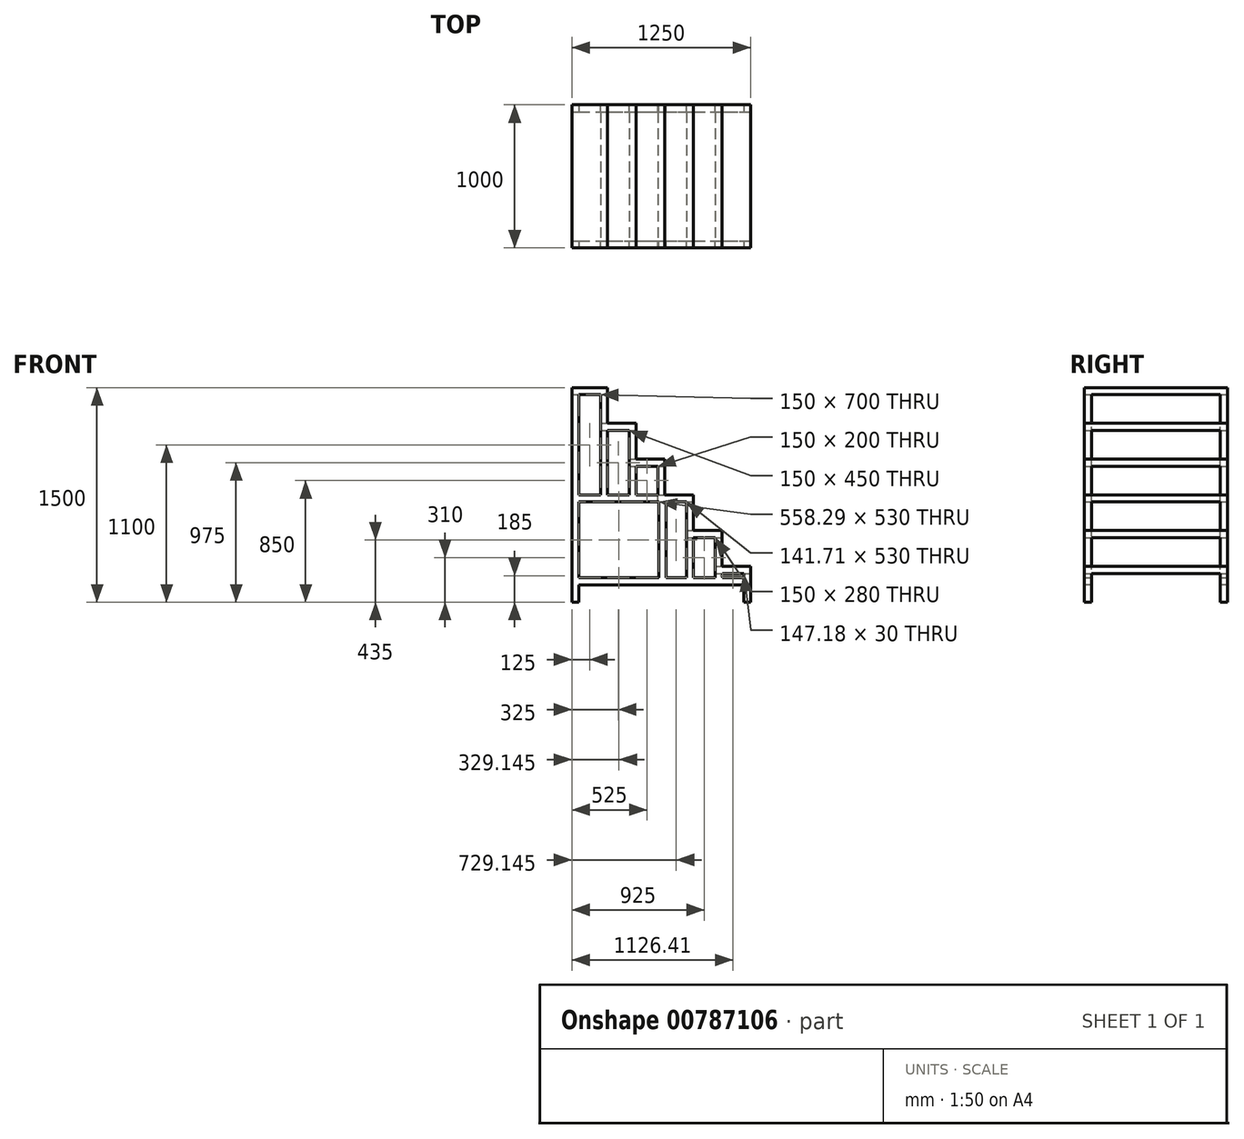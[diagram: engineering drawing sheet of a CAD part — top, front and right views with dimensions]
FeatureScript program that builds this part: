
annotation { "Feature Type Name" : "Feature", "Feature Type Description" : "" }
export const myFeature = defineFeature(function(context is Context, id is Id, definition is map)
    precondition{}
    {
        {
            var Q0;
            Q0=qCreatedBy(makeId("Front.planeOp"),FACE);
            var sketch = newSketch(context, id + "F0", { "sketchPlane" : qUnion([Q0])});
            skLineSegment(sketch, "E0.bottom", {"start": v(0, 0) * mm, "end": v(1250, 0) * mm});
            skLineSegment(sketch, "E0.top", {"start": v(0, 250) * mm, "end": v(1250, 250) * mm});
            skLineSegment(sketch, "E0.left", {"start": v(0, 0) * mm, "end": v(0, 250) * mm});
            skLineSegment(sketch, "E0.right", {"start": v(1250, 0) * mm, "end": v(1250, 250) * mm});
            skLineSegment(sketch, "E1.bottom", {"start": v(0, 250) * mm, "end": v(1050, 250) * mm});
            skLineSegment(sketch, "E1.top", {"start": v(0, 500) * mm, "end": v(1050, 500) * mm});
            skLineSegment(sketch, "E1.left", {"start": v(0, 250) * mm, "end": v(0, 500) * mm});
            skLineSegment(sketch, "E1.right", {"start": v(1050, 250) * mm, "end": v(1050, 500) * mm});
            skLineSegment(sketch, "E2.bottom", {"start": v(0, 500) * mm, "end": v(850, 500) * mm});
            skLineSegment(sketch, "E2.top", {"start": v(0, 750) * mm, "end": v(850, 750) * mm});
            skLineSegment(sketch, "E2.left", {"start": v(0, 500) * mm, "end": v(0, 750) * mm});
            skLineSegment(sketch, "E2.right", {"start": v(850, 500) * mm, "end": v(850, 750) * mm});
            skLineSegment(sketch, "E3.bottom", {"start": v(0, 750) * mm, "end": v(650, 750) * mm});
            skLineSegment(sketch, "E3.top", {"start": v(0, 1000) * mm, "end": v(650, 1000) * mm});
            skLineSegment(sketch, "E3.left", {"start": v(0, 750) * mm, "end": v(0, 1000) * mm});
            skLineSegment(sketch, "E3.right", {"start": v(650, 750) * mm, "end": v(650, 1000) * mm});
            skLineSegment(sketch, "E4.bottom", {"start": v(0, 1000) * mm, "end": v(450, 1000) * mm});
            skLineSegment(sketch, "E4.top", {"start": v(0, 1250) * mm, "end": v(450, 1250) * mm});
            skLineSegment(sketch, "E4.left", {"start": v(0, 1000) * mm, "end": v(0, 1250) * mm});
            skLineSegment(sketch, "E4.right", {"start": v(450, 1000) * mm, "end": v(450, 1250) * mm});
            skLineSegment(sketch, "E5.bottom", {"start": v(0, 1250) * mm, "end": v(250, 1250) * mm});
            skLineSegment(sketch, "E5.top", {"start": v(0, 1500) * mm, "end": v(250, 1500) * mm});
            skLineSegment(sketch, "E5.left", {"start": v(0, 1250) * mm, "end": v(0, 1500) * mm});
            skLineSegment(sketch, "E5.right", {"start": v(250, 1250) * mm, "end": v(250, 1500) * mm});
            skSolve(sketch);
        }
        {
            var Q0;
            Q0 = qSketchRegion(id + "F0", true);
            extrude(context, id + "F1", {"entities" : qUnion([Q0]), "depth" : 1000 * mm, "offsetDistance" : 25 * mm});
        }
        {
            var Q0;
            Q0=makeQuery(id+"F1.opExtrude","SWEPT_FACE",FACE,{"disambiguationData":[OSD([sQuery(id+"F0.wireOp",EDGE,"E0.left"),sQuery(id+"F0.wireOp",EDGE,"E1.left"),sQuery(id+"F0.wireOp",EDGE,"E2.left"),sQuery(id+"F0.wireOp",EDGE,"E3.left"),sQuery(id+"F0.wireOp",EDGE,"E4.left"),sQuery(id+"F0.wireOp",EDGE,"E5.left")])]});
            shell(context, id + "F2", {"entities" : qUnion([Q0]), "thickness" : 50 * mm});
        }
        {
            var Q0;
            Q0=makeQuery(id+"F1.opExtrude","CAP_FACE",FACE,{"disambiguationData":[OSD([sQuery(id+"F0.wireOp",EDGE,"E0.bottom"),sQuery(id+"F0.wireOp",EDGE,"E0.top"),sQuery(id+"F0.wireOp",EDGE,"E0.left"),sQuery(id+"F0.wireOp",EDGE,"E0.right"),sQuery(id+"F0.wireOp",EDGE,"E1.top"),sQuery(id+"F0.wireOp",EDGE,"E1.left"),sQuery(id+"F0.wireOp",EDGE,"E1.right"),sQuery(id+"F0.wireOp",EDGE,"E2.top"),sQuery(id+"F0.wireOp",EDGE,"E2.left"),sQuery(id+"F0.wireOp",EDGE,"E2.right"),sQuery(id+"F0.wireOp",EDGE,"E3.top"),sQuery(id+"F0.wireOp",EDGE,"E3.left"),sQuery(id+"F0.wireOp",EDGE,"E3.right"),sQuery(id+"F0.wireOp",EDGE,"E4.top"),sQuery(id+"F0.wireOp",EDGE,"E4.left"),sQuery(id+"F0.wireOp",EDGE,"E4.right"),sQuery(id+"F0.wireOp",EDGE,"E5.top"),sQuery(id+"F0.wireOp",EDGE,"E5.left"),sQuery(id+"F0.wireOp",EDGE,"E5.right")])],"isStart":false});
            var sketch = newSketch(context, id + "F3", { "sketchPlane" : qUnion([Q0])});
            skLineSegment(sketch, "E6.bottom", {"start": v(50, 0) * mm, "end": v(1200, 0) * mm});
            skLineSegment(sketch, "E6.top", {"start": v(50, 120) * mm, "end": v(1200, 120) * mm});
            skLineSegment(sketch, "E6.left", {"start": v(50, 0) * mm, "end": v(50, 120) * mm});
            skLineSegment(sketch, "E6.right", {"start": v(1200, 0) * mm, "end": v(1200, 120) * mm});
            skSolve(sketch);
        }
        {
            var Q0;
            Q0=makeQuery(id+"F3.imprint","IMPRINT",FACE,{"disambiguationData":[TD([[makeQuery(id+"F3.imprint","IMPRINT",EDGE,{"derivedFrom":sQuery(id+"F3.wireOp",EDGE,"E6.bottom")}),1.0]])]});
            extrude(context, id + "F4", {"entities" : qUnion([Q0]), "operationType" : NewBodyOperationType.REMOVE, "oppositeDirection" : true, "depth" : 1100 * mm, "offsetDistance" : 25 * mm});
        }
        {
            var Q0;
            Q0=makeQuery(id+"F1.opExtrude","SWEPT_FACE",FACE,{"disambiguationData":[OSD([sQuery(id+"F0.wireOp",EDGE,"E0.right")])]});
            var sketch = newSketch(context, id + "F5", { "sketchPlane" : qUnion([Q0])});
            skLineSegment(sketch, "E7.bottom", {"start": v(-950, 0) * mm, "end": v(-50, 0) * mm});
            skLineSegment(sketch, "E7.top", {"start": v(-950, 200) * mm, "end": v(-50, 200) * mm});
            skLineSegment(sketch, "E7.left", {"start": v(-950, 0) * mm, "end": v(-950, 200) * mm});
            skLineSegment(sketch, "E7.right", {"start": v(-50, 0) * mm, "end": v(-50, 200) * mm});
            skSolve(sketch);
        }
        {
            var Q0;
            Q0 = qSketchRegion(id + "F5", true);
            extrude(context, id + "F6", {"entities" : qUnion([Q0]), "operationType" : NewBodyOperationType.REMOVE, "oppositeDirection" : true, "depth" : 5000 * mm, "offsetDistance" : 25 * mm});
        }
        {
            var Q0;
            Q0=makeQuery(id+"F1.opExtrude","SWEPT_FACE",FACE,{"disambiguationData":[OSD([sQuery(id+"F0.wireOp",EDGE,"E1.right")])]});
            var sketch = newSketch(context, id + "F7", { "sketchPlane" : qUnion([Q0])});
            skLineSegment(sketch, "E8.bottom", {"start": v(-950, 250) * mm, "end": v(-50, 250) * mm});
            skLineSegment(sketch, "E8.top", {"start": v(-950, 450) * mm, "end": v(-50, 450) * mm});
            skLineSegment(sketch, "E8.left", {"start": v(-950, 250) * mm, "end": v(-950, 450) * mm});
            skLineSegment(sketch, "E8.right", {"start": v(-50, 250) * mm, "end": v(-50, 450) * mm});
            skSolve(sketch);
        }
        {
            var Q0;
            Q0 = qSketchRegion(id + "F7", true);
            extrude(context, id + "F8", {"entities" : qUnion([Q0]), "operationType" : NewBodyOperationType.REMOVE, "oppositeDirection" : true, "depth" : 300 * mm, "offsetDistance" : 25 * mm});
        }
        {
            var Q0;
            Q0=makeQuery(id+"F1.opExtrude","SWEPT_FACE",FACE,{"disambiguationData":[OSD([sQuery(id+"F0.wireOp",EDGE,"E2.right")])]});
            var sketch = newSketch(context, id + "F9", { "sketchPlane" : qUnion([Q0])});
            skLineSegment(sketch, "E9.bottom", {"start": v(-950, 500) * mm, "end": v(-50, 500) * mm});
            skLineSegment(sketch, "E9.top", {"start": v(-950, 700) * mm, "end": v(-50, 700) * mm});
            skLineSegment(sketch, "E9.left", {"start": v(-950, 500) * mm, "end": v(-950, 700) * mm});
            skLineSegment(sketch, "E9.right", {"start": v(-50, 500) * mm, "end": v(-50, 700) * mm});
            skSolve(sketch);
        }
        {
            var Q0;
            Q0 = qSketchRegion(id + "F9", true);
            extrude(context, id + "F10", {"entities" : qUnion([Q0]), "operationType" : NewBodyOperationType.REMOVE, "oppositeDirection" : true, "depth" : 300 * mm, "offsetDistance" : 25 * mm});
        }
        {
            var Q0;
            Q0=makeQuery(id+"F1.opExtrude","SWEPT_FACE",FACE,{"disambiguationData":[OSD([sQuery(id+"F0.wireOp",EDGE,"E3.right")])]});
            var sketch = newSketch(context, id + "F11", { "sketchPlane" : qUnion([Q0])});
            skLineSegment(sketch, "E10.bottom", {"start": v(-950, 750) * mm, "end": v(-50, 750) * mm});
            skLineSegment(sketch, "E10.top", {"start": v(-950, 950) * mm, "end": v(-50, 950) * mm});
            skLineSegment(sketch, "E10.left", {"start": v(-950, 750) * mm, "end": v(-950, 950) * mm});
            skLineSegment(sketch, "E10.right", {"start": v(-50, 750) * mm, "end": v(-50, 950) * mm});
            skSolve(sketch);
        }
        {
            var Q0;
            Q0 = qSketchRegion(id + "F11", true);
            extrude(context, id + "F12", {"entities" : qUnion([Q0]), "operationType" : NewBodyOperationType.REMOVE, "oppositeDirection" : true, "depth" : 300 * mm, "offsetDistance" : 25 * mm});
        }
        {
            var Q0;
            Q0=makeQuery(id+"F1.opExtrude","SWEPT_FACE",FACE,{"disambiguationData":[OSD([sQuery(id+"F0.wireOp",EDGE,"E4.right")])]});
            var sketch = newSketch(context, id + "F13", { "sketchPlane" : qUnion([Q0])});
            skLineSegment(sketch, "E11.bottom", {"start": v(-950, 1000) * mm, "end": v(-50, 1000) * mm});
            skLineSegment(sketch, "E11.top", {"start": v(-950, 1200) * mm, "end": v(-50, 1200) * mm});
            skLineSegment(sketch, "E11.left", {"start": v(-950, 1000) * mm, "end": v(-950, 1200) * mm});
            skLineSegment(sketch, "E11.right", {"start": v(-50, 1000) * mm, "end": v(-50, 1200) * mm});
            skSolve(sketch);
        }
        {
            var Q0;
            Q0 = qSketchRegion(id + "F13", true);
            extrude(context, id + "F14", {"entities" : qUnion([Q0]), "operationType" : NewBodyOperationType.REMOVE, "oppositeDirection" : true, "depth" : 300 * mm, "offsetDistance" : 25 * mm});
        }
        {
            var Q0;
            Q0=makeQuery(id+"F1.opExtrude","SWEPT_FACE",FACE,{"disambiguationData":[OSD([sQuery(id+"F0.wireOp",EDGE,"E5.right")])]});
            var sketch = newSketch(context, id + "F15", { "sketchPlane" : qUnion([Q0])});
            skLineSegment(sketch, "E12.bottom", {"start": v(-950, 1250) * mm, "end": v(-50, 1250) * mm});
            skLineSegment(sketch, "E12.top", {"start": v(-950, 1450) * mm, "end": v(-50, 1450) * mm});
            skLineSegment(sketch, "E12.left", {"start": v(-950, 1250) * mm, "end": v(-950, 1450) * mm});
            skLineSegment(sketch, "E12.right", {"start": v(-50, 1250) * mm, "end": v(-50, 1450) * mm});
            skSolve(sketch);
        }
        {
            var Q0;
            Q0 = qSketchRegion(id + "F15", true);
            extrude(context, id + "F16", {"entities" : qUnion([Q0]), "operationType" : NewBodyOperationType.REMOVE, "oppositeDirection" : true, "depth" : 300 * mm, "offsetDistance" : 25 * mm});
        }
        {
            var Q0;
            Q0=makeQuery(id+"F1.opExtrude","CAP_FACE",FACE,{"disambiguationData":[OSD([sQuery(id+"F0.wireOp",EDGE,"E0.bottom"),sQuery(id+"F0.wireOp",EDGE,"E0.top"),sQuery(id+"F0.wireOp",EDGE,"E0.left"),sQuery(id+"F0.wireOp",EDGE,"E0.right"),sQuery(id+"F0.wireOp",EDGE,"E1.top"),sQuery(id+"F0.wireOp",EDGE,"E1.left"),sQuery(id+"F0.wireOp",EDGE,"E1.right"),sQuery(id+"F0.wireOp",EDGE,"E2.top"),sQuery(id+"F0.wireOp",EDGE,"E2.left"),sQuery(id+"F0.wireOp",EDGE,"E2.right"),sQuery(id+"F0.wireOp",EDGE,"E3.top"),sQuery(id+"F0.wireOp",EDGE,"E3.left"),sQuery(id+"F0.wireOp",EDGE,"E3.right"),sQuery(id+"F0.wireOp",EDGE,"E4.top"),sQuery(id+"F0.wireOp",EDGE,"E4.left"),sQuery(id+"F0.wireOp",EDGE,"E4.right"),sQuery(id+"F0.wireOp",EDGE,"E5.top"),sQuery(id+"F0.wireOp",EDGE,"E5.left"),sQuery(id+"F0.wireOp",EDGE,"E5.right")])],"isStart":true});
            var sketch = newSketch(context, id + "F17", { "sketchPlane" : qUnion([Q0])});
            skLineSegment(sketch, "E13", {"start": v(-600, 750) * mm, "end": v(-450, 750) * mm});
            skLineSegment(sketch, "E14", {"start": v(-50, 750) * mm, "end": v(-50, 1450) * mm});
            skLineSegment(sketch, "E15", {"start": v(-50, 1450) * mm, "end": v(-200, 1450) * mm});
            skLineSegment(sketch, "E16", {"start": v(-200, 1450) * mm, "end": v(-200, 1200) * mm});
            skLineSegment(sketch, "E17", {"start": v(-250, 1200) * mm, "end": v(-400, 1200) * mm});
            skLineSegment(sketch, "E18", {"start": v(-400, 1200) * mm, "end": v(-400, 950) * mm});
            skLineSegment(sketch, "E19", {"start": v(-450, 950) * mm, "end": v(-600, 950) * mm});
            skLineSegment(sketch, "E20", {"start": v(-600, 950) * mm, "end": v(-600, 750) * mm});
            skLineSegment(sketch, "E21", {"start": v(-608.29, 700) * mm, "end": v(-50, 700) * mm});
            skLineSegment(sketch, "E22", {"start": v(-400, 950) * mm, "end": v(-400, 750) * mm});
            skLineSegment(sketch, "E23", {"start": v(-450, 950) * mm, "end": v(-450, 750) * mm});
            skLineSegment(sketch, "E24", {"start": v(-200, 1200) * mm, "end": v(-200, 750) * mm});
            skLineSegment(sketch, "E25", {"start": v(-250, 1200) * mm, "end": v(-250, 750) * mm});
            skLineSegment(sketch, "E26", {"start": v(-800, 700) * mm, "end": v(-800, 450) * mm});
            skLineSegment(sketch, "E27", {"start": v(-850, 450) * mm, "end": v(-1000, 450) * mm});
            skLineSegment(sketch, "E28", {"start": v(-1000, 450) * mm, "end": v(-1000, 200) * mm});
            skLineSegment(sketch, "E29", {"start": v(-1052.82, 200) * mm, "end": v(-1200, 200) * mm});
            skLineSegment(sketch, "E30", {"start": v(-1200, 200) * mm, "end": v(-1200, 170) * mm});
            skLineSegment(sketch, "E31", {"start": v(-1200, 170) * mm, "end": v(-1052.82, 170) * mm});
            skLineSegment(sketch, "E32", {"start": v(-50, 170) * mm, "end": v(-50, 700) * mm});
            skLineSegment(sketch, "E33", {"start": v(-658.29, 700) * mm, "end": v(-658.29, 170) * mm});
            skLineSegment(sketch, "E34", {"start": v(-608.29, 700) * mm, "end": v(-608.29, 170) * mm});
            skLineSegment(sketch, "E35", {"start": v(-800, 450) * mm, "end": v(-800, 170) * mm});
            skLineSegment(sketch, "E36", {"start": v(-850, 450) * mm, "end": v(-850, 170) * mm});
            skLineSegment(sketch, "E37", {"start": v(-1000, 200) * mm, "end": v(-1000, 170) * mm});
            skLineSegment(sketch, "E38", {"start": v(-1052.82, 200) * mm, "end": v(-1052.82, 170) * mm});
            skLineSegment(sketch, "E39", {"start": v(-800, 700) * mm, "end": v(-658.29, 700) * mm});
            skPoint(sketch, "E40.orphan", {"position": v(0, 700) * mm});
            skPoint(sketch, "E41.orphan", {"position": v(0, 750) * mm});
            skLineSegment(sketch, "E42.trimOffspring", {"start": v(-200, 750) * mm, "end": v(-50, 750) * mm});
            skLineSegment(sketch, "E43.trimOffspring", {"start": v(-400, 750) * mm, "end": v(-250, 750) * mm});
            skLineSegment(sketch, "E44.trimOffspring", {"start": v(-608.29, 170) * mm, "end": v(-50, 170) * mm});
            skLineSegment(sketch, "E45.trimOffspring", {"start": v(-800, 170) * mm, "end": v(-658.29, 170) * mm});
            skLineSegment(sketch, "E46.trimOffspring", {"start": v(-1000, 170) * mm, "end": v(-850, 170) * mm});
            skSolve(sketch);
        }
        {
            var Q0;
            Q0 = qSketchRegion(id + "F17", true);
            extrude(context, id + "F18", {"entities" : qUnion([Q0]), "operationType" : NewBodyOperationType.REMOVE, "oppositeDirection" : true, "depth" : 5000 * mm, "offsetDistance" : 25 * mm});
        }
    });
